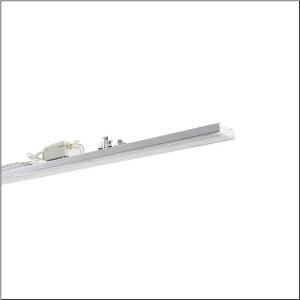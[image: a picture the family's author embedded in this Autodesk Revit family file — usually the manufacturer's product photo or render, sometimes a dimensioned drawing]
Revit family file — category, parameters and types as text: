
# Revit family: licross_r__11_recessed_ho_51tl12dv4m2m3s_8b63
name_source: partatom
category: Lighting Fixtures
units: mm (PartAtom-declared; Revit-internal decimal feet)

## family parameters
Cut with Voids When Loaded = No
Host = Face
Light Source = No
Part Type = Normal
Room Calculation Point = No
Round Connector Dimension = Use Diameter
Shared = No

## types (1)
- --- (1 x LED, 1010 lm, 5.9 W, 4000K)
    Apparent Load = 6 VA
    CIE Flux Codes = 66 91 98 100 100
    Color Rendering = 80
    Color Temperature = 4000K
    Default Elevation = 1800 mm
    Description = Licross® 11 Recessed HO, luminaire insert, of sheet steel, coil coated, white, length: 2.250mm, width: 66mm, height: 67mm, LED rated luminous flux: 27.150lm, light colour: 840, control gear: DALI 2 (for two DALI lines), with plug, 6-pole, with phase selection, for trunking rail, 14-core, mains connection: 220..240V, AC, 50/60Hz, rated input power: 154W, for trunking rail, 14-core, halogen-free wiring, for emergency light function, converter,control gear: single battery element, battery: LiFePO4, 9Ah, primary optical cover: cover, of PMMA, light emission: direct distribution, primary light characteristic: symmetric, protection rating (complete): IP40, insulation class (complete): insulation class I (protective earthing), certification: CE, UKCA, protection symbol: D if used in an environment without relevant dust loads with corresponding accessories, impact resistance: IK06, permissible ambient temperature for indoor applications: +5..+35°C, standard: EN 60598-2-22, LABS conformity tested according to VDMA 24364:2018-05, reducing of maximum allowable ambient temperature of 5°C with ceiling mounting, corresponds to IFS (International Featured Standards) requirements for safety and quality in the food industry, packaging unit: 1 piece
    Height = 58 mm
    Lamp = 1 x LED
    Lamp Light Flux = 1010 lm
    Lamp Power = 5.9 W
    Lamp count = 1
    Length = 2250 mm
    Luminous efficacy = 171 lm/W
    Manufacturer = Siteco
    ModVariant = No
    Model = 51TL12DV4M2M3S
    Mounting Place = Ceiling
    Mounting Type = Pendant
    Number of Poles = 1
    OnlyDefault = Yes
    Power Factor = 1
    Product Name = Licross® 11 Recessed HO
    Product group = luminaire insert
    ProductGroupID = 901
    Protection Class = Protection class I
    Protection Degree = IP 40
    RLX_Detail_Level = 1
    RLX_Emergency_Light_Flux = 0 lm
    RLX_Emergency_Type = 0
    RLX_Emergency_Type_DB = No
    RlxData = <blob elided: 30021 chars, md5=584ffc55>
    Socket = socket
    Standby Power = 0 W
    System Light Flux = 1010 lm
    System Power = 6 W
    Type Comments = : emergency light operation: 3 h
    Type Image = l_1296930.jpg
    URL = http://relux.com
    VarID = @adj_054135
    Voltage = 0 V
    Weight = 0.00 kg
    Width = 66 mm

## geometry (parser evidence)
native form markers: Blend x4, Sweep x9
no freeform markers — native parametric forms only
